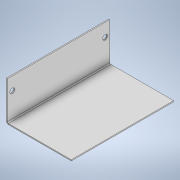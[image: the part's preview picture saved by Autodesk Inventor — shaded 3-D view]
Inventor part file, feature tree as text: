
AUTODESK INVENTOR PART (.ipt)
format: ipt  version: 2022 (Build 260153000, 153)  size: 142,336 bytes
history: native  units: in
note: dims shown in document units (in); Inventor stores cm internally (conversion verified against a paired STEP export)
features: other x4, sketch x4, hole x2
ambient origin geometry x8: Origin, YZ Plane, XZ Plane, XY Plane, X Axis, Y Axis, Z Axis, Center Point
bodies: Body1 (feature_tree)
feature tree (10):
  other  "Sólido1"
  other  "Cara1"
  other  "Pliegue1"
  hole  "Agujero3"  [1 undecoded]
  hole  "Agujero4"  [1 undecoded]
  sketch  "Boceto1"  dims[d0=3.7795in d1=3.7795in]
  other  "Placa1"
  sketch  "Boceto4"  dims[d2=0.0394in d3=2.3622in]
  sketch  "Boceto7"  dims[d4=2.3622in]
  sketch  "Boceto8"  dims[d5=0.0394in d6=0.0197in d7=0.0787in d8=0.0394in d9=90.0deg d10=0.0394in d11=0.1772in d12=0.4724in d13=0.1772in d14=0.1772in d15=0.4724in d16=0.1772in d24=0.1772in d25=0.4724in d26=0.1772in d36=0.4724in d37=0.1772in d38=0.1772in d39=0.2362in d40=0.1575in d41=0.0787in d42=90.0deg d43=0.315in d44=0.8108in d45=0.4724in d46=0.1772in d47=0.1772in d48=0.2362in d49=0.1575in d50=0.0787in d51=90.0deg d52=0.315in d53=0.8108in]
note: 2 required parameter values undecoded (feature->parameter linkage not recoverable at this tier; creation-order binding heuristic only, values carry confidence <= 0.55)
